# Revit family: Accessory-Teknion-EMDS_Desktop_Shelf-R2016
name_source: partatom
category: Furniture
revit_build: Autodesk Revit 2018 (Build: 20190510_1515(x64)
units: mm (PartAtom-declared; Revit-internal decimal feet)

## family parameters
Always vertical = Yes
Cut with Voids When Loaded = No
OmniClass Number = 23.40.20.00
OmniClass Title = General Furniture and Specialties
Room Calculation Point = No
Shared = Yes
Work Plane-Based = Yes

## types (7) — shared parameters
Assembly Code = E2020200
Default Elevation = 48 "
Manufacturer = Teknion
Manufacturer Fax = 416.661.4586
Part Number = EMDS
Product Documentation Link = https://assets.teknion.com
Product Line = Emote
Product Page URL = https://www.teknion.com
Series = Emote
Sustainability Data = https://www.teknion.com
URL = www.teknion.com
Unit Weight URL = http://www.teknion.com
Warranty = http://www.teknion.com

## per-type parameters (varying)
| type | Description | Foot Offset | Model | Width |
| 24" Width | Emote Desktop Shelf, 24" Width | 5.373 " | EMDS24 | 24 " |
| 30" Width | Emote Desktop Shelf, 30" Width | 5.373 " | EMDS30 | 30 " |
| 36" Width | Emote Desktop Shelf, 36" Width | 5.373 " | EMDS36 | 36 " |
| 42" Width | Emote Desktop Shelf, 42" Width | 10.248 " | EMDS42 | 42 " |
| 48" Width | Emote Desktop Shelf, 48" Width | 10.248 " | EMDS48 | 48 " |
| 54" Width | Emote Desktop Shelf, 54" Width | 10.248 " | EMDS54 | 54 " |
| 60" Width | Emote Desktop Shelf, 60" Width | 10.252 " | EMDS60 | 60 " |

## geometry (parser evidence)
native form markers: Blend x47, Sweep x2
no freeform markers — native parametric forms only
